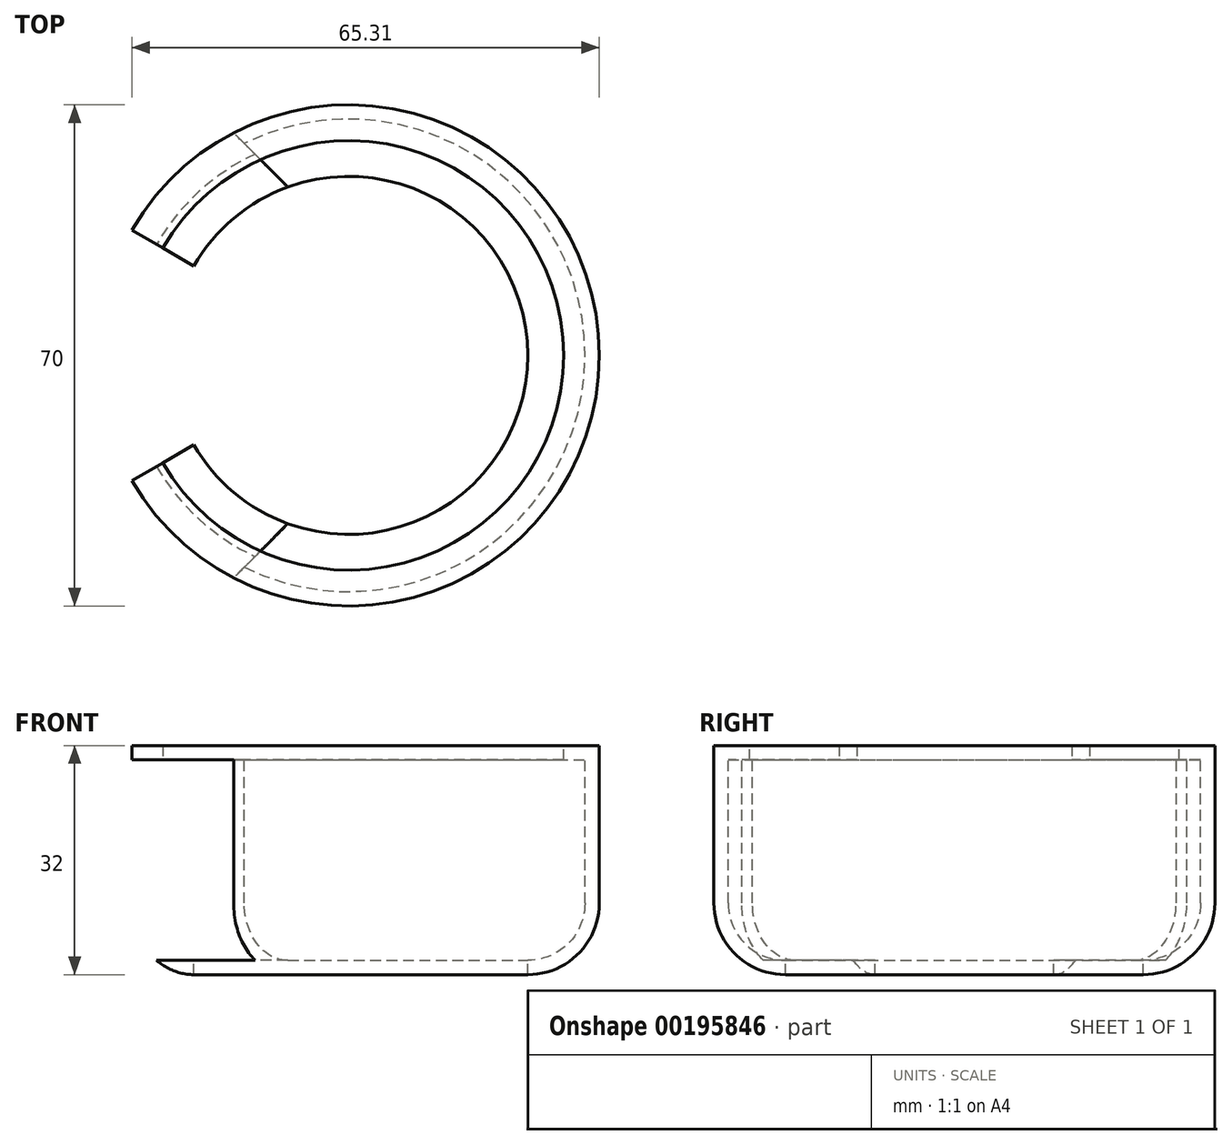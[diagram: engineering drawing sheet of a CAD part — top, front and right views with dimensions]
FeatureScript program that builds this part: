
annotation { "Feature Type Name" : "Feature", "Feature Type Description" : "" }
export const myFeature = defineFeature(function(context is Context, id is Id, definition is map)
    precondition{}
    {
        {
            var Q0;
            Q0=qCreatedBy(makeId("Front.planeOp"),FACE);
            var sketch = newSketch(context, id + "F0", { "sketchPlane" : qUnion([Q0])});
            skLineSegment(sketch, "E0", {"start": v(35, 0) * mm, "end": v(35, -20) * mm});
            skArc(sketch, "E1", {"start": v(35, -20) * mm, "mid": v(32.07, -27.07) * mm, "end": v(25, -30) * mm});
            skLineSegment(sketch, "E2", {"start": v(35, 0) * mm, "end": v(35, 2) * mm});
            skLineSegment(sketch, "E3", {"start": v(35, 2) * mm, "end": v(30, 2) * mm});
            skLineSegment(sketch, "E4", {"start": v(30, 2) * mm, "end": v(30, 0) * mm});
            skLineSegment(sketch, "E5", {"start": v(30, 0) * mm, "end": v(33, 0) * mm});
            skLineSegment(sketch, "E6", {"start": v(33, 0) * mm, "end": v(33, -20) * mm});
            skArc(sketch, "E7", {"start": v(33, -20) * mm, "mid": v(30.66, -25.66) * mm, "end": v(25, -28) * mm});
            skLineSegment(sketch, "E8", {"start": v(25, -30) * mm, "end": v(25, -28) * mm});
            skLineSegment(sketch, "E9", {"start": v(0, 0) * mm, "end": v(0, -30) * mm});
            skSolve(sketch);
        }
        {
            var Q0;
            Q0=makeQuery(id+"F0.imprint","IMPRINT",FACE,{"disambiguationData":[TD([[makeQuery(id+"F0.imprint","IMPRINT",EDGE,{"derivedFrom":sQuery(id+"F0.wireOp",EDGE,"E0")}),-1.0]])]});
            var Q1;
            Q1=sQuery(id+"F0.wireOp",EDGE,"E9");
            revolve(context, id + "F1", {"entities" : qUnion([Q0]), "axis" : qUnion([Q1]), "revolveType" : RevolveType.SYMMETRIC, "angle" : 300 * degree});
        }
        {
            var Q0;
            Q0=qCreatedBy(makeId("Top.planeOp"),FACE);
            var sketch = newSketch(context, id + "F2", { "sketchPlane" : qUnion([Q0])});
            skLineSegment(sketch, "E10", {"start": v(15, 0) * mm, "end": v(-55, 70) * mm});
            skLineSegment(sketch, "E11", {"start": v(-55, 70) * mm, "end": v(-55, 0) * mm});
            skLineSegment(sketch, "E12.MirrorCS", {"start": v(-55, -70) * mm, "end": v(-55, 0) * mm});
            skLineSegment(sketch, "E13.MirrorCS", {"start": v(15, 0) * mm, "end": v(-55, -70) * mm});
            skSolve(sketch);
        }
        {
            var Q0;
            Q0=makeQuery(id+"F2.imprint","IMPRINT",FACE,{"disambiguationData":[TD([[makeQuery(id+"F2.imprint","IMPRINT",EDGE,{"derivedFrom":sQuery(id+"F2.wireOp",EDGE,"E10")}),1.0]])]});
            var Q1;
            Q1=makeQuery(id+"F1.opRevolve","SWEPT_FACE",FACE,{"disambiguationData":[OSD([sQuery(id+"F0.wireOp",EDGE,"E7")])]});
            extrude(context, id + "F3", {"entities" : qUnion([Q0]), "operationType" : NewBodyOperationType.REMOVE, "oppositeDirection" : true, "endBoundEntityFace" : qUnion([Q1]), "depth" : 28 * mm});
        }
    });
